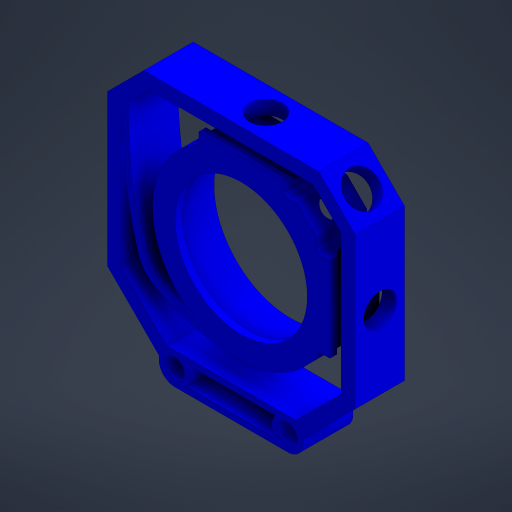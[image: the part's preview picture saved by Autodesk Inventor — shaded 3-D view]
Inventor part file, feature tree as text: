
AUTODESK INVENTOR PART (.ipt)
format: ipt  version: 2023.4 (Build 274418000, 418)  size: 445,440 bytes
history: native  units: mm
features: extrude x6, projected_geometry x4, reference x4, other x3, plane x1, mirror x1, chamfer x1, sketch x1
ambient origin geometry x8: Origin, YZ Plane, XZ Plane, XY Plane, X Axis, Y Axis, Z Axis, Center Point
bodies: Solid1 (feature_tree)
feature tree (21):
  extrude  "Extrusion1"  TaperAngle=45.0deg  [1 undecoded]
  extrude  "Extrusion2"  Depth=1.25mm
  extrude  "Extrusion3"  Depth=1.25mm
  extrude  "Extrusion4"  Depth=1.25mm
  plane  "Work Plane1"
  mirror  "Mirror1"
  extrude  "Extrusion5"  Depth=1.25mm
  extrude  "Extrusion6"  Depth=1.25mm
  chamfer  "Chamfer1"  Distance=2.0mm
  sketch  "Sketch1"  dims[d2=2.5mm d3=45.0deg d4=27.15mm d5=2.5mm d6=2.125mm d7=1.0mm d8=15.0mm d9=2.0mm d10=0.625mm d11=5.0mm d12=135.0deg d13=3.0mm d14=2.0mm d15=2.0mm d16=38.935534mm d17=38.935534mm d18=9.25mm d19=9.25mm d20=9.25mm d21=9.25mm d22=5.0mm d23=5.0mm d24=5.0mm d25=5.0mm d26=2.5mm d28=8.75mm d29=0.0mm d30=1.875mm d31=1.25mm d32=0.0mm d33=5.75mm d34=10.0mm d35=0.0mm d36=1.25mm d37=135.0deg d38=10.0mm d39=0.0mm d40=3.75mm d41=6.0mm d42=10.0mm d43=0.0mm d44=10.0mm d45=0.0mm d48=17.5mm d49=5.0mm d50=1.25mm d51=2.5mm d52=2.5mm d53=1.075mm d54=2.0mm d55=45.0deg d56=0.1425mm d57=0.1425mm d58=1.25mm d60=1.25mm]
  projected_geometry  "Projected Loop1"
  projected_geometry  "Projected Loop2"
  projected_geometry  "Projected Loop3"
  projected_geometry  "Projected Loop4"
  reference  "Reference4"
  reference  "Reference5"
  reference  "Reference6"
  reference  "Reference7"
  other  "<path>\Projects\Project Protocube\Protocube\CAD, STL, OBJ Files\1 CAD\Cube 1x1 V5.iam"
  other  "Cube 1x1 V5.iam"
  other  "Cube 1x1 Bottom V5 Closed Slotted:1"
note: 1 required parameter value undecoded (feature->parameter linkage not recoverable at this tier; creation-order binding heuristic only, values carry confidence <= 0.55)
note: 1 file-system path scrubbed to <path> (originals preserved in map.json)
